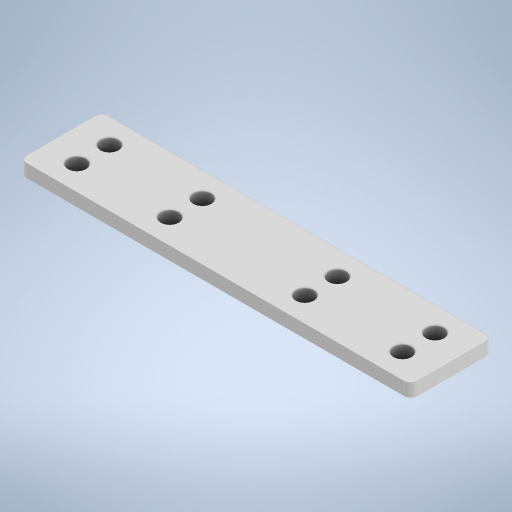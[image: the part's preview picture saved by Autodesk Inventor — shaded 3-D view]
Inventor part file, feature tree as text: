
AUTODESK INVENTOR PART (.ipt)
format: ipt  version: 2024.2 (Build 282272000, 272)  size: 280,064 bytes
history: native  units: mm
features: other x1, extrude x1, fillet x1, sketch x1
ambient origin geometry x8: Origin, YZ Plane, XZ Plane, XY Plane, X Axis, Y Axis, Z Axis, Center Point
bodies: Body1 (feature_tree)
feature tree (4):
  other  "Bryła1"
  extrude  "Wyciągnięcie proste1"  Depth=80.0mm
  fillet  "Zaokrąglenie1"  Radius=25.0mm
  sketch  "Szkic1"
